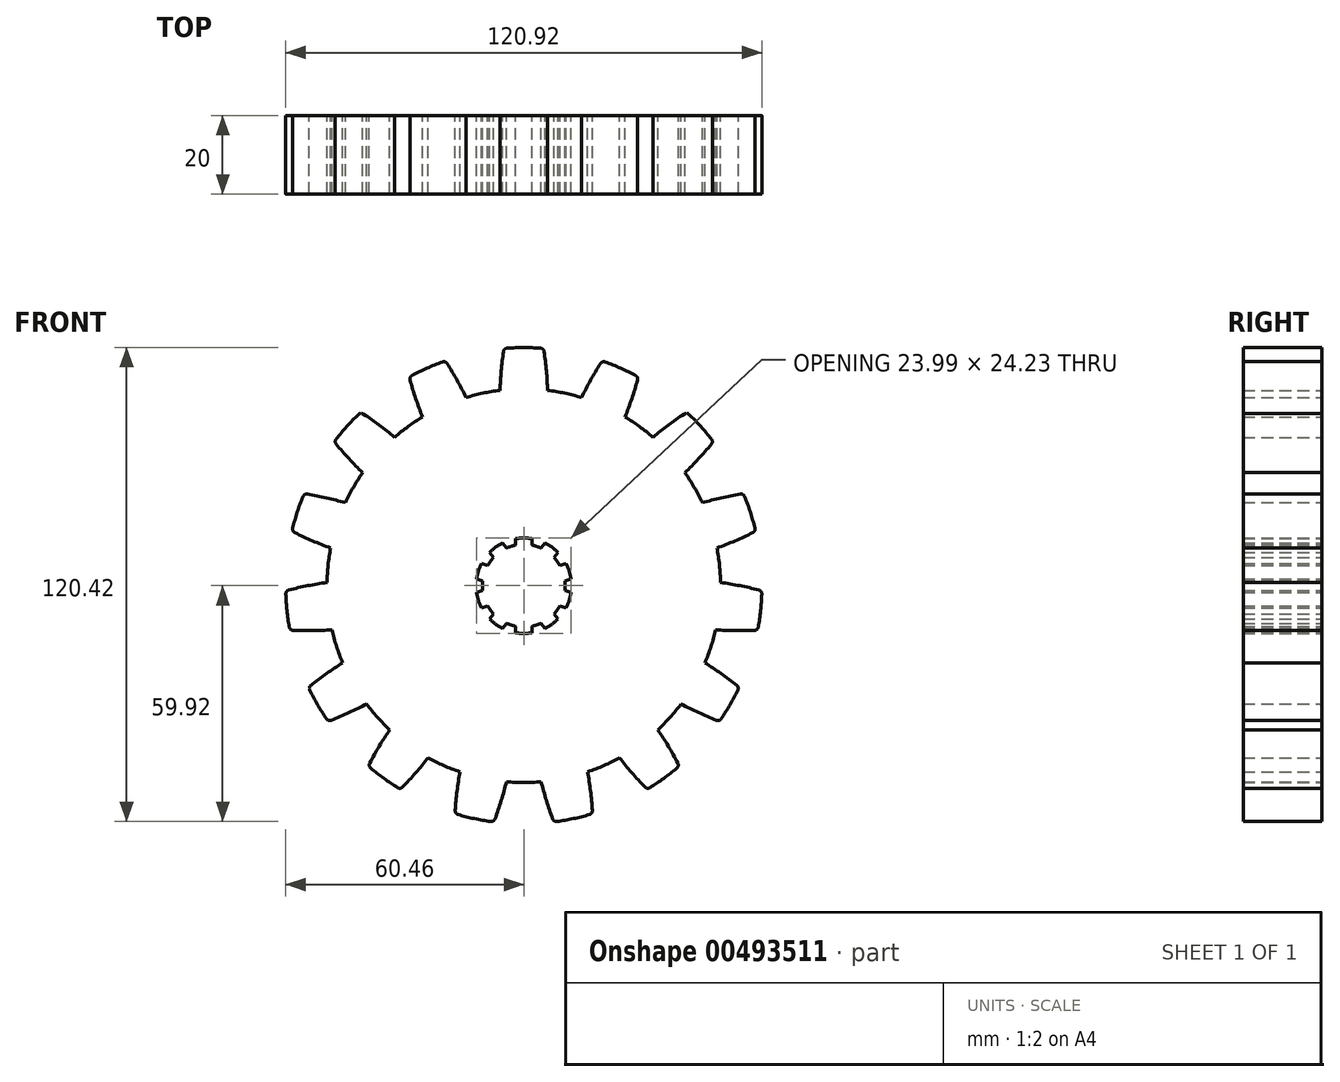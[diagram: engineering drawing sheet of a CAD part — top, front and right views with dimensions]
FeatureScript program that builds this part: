
annotation { "Feature Type Name" : "Feature", "Feature Type Description" : "" }
export const myFeature = defineFeature(function(context is Context, id is Id, definition is map)
    precondition{}
    {
        {
            var Q0;
            Q0=qCreatedBy(makeId("Front.planeOp"),FACE);
            var sketch = newSketch(context, id + "F0", { "sketchPlane" : qUnion([Q0])});
            skCircle(sketch, "E0", {"center": v(0, 0) * mm, "radius": 50 * mm});
            skCircle(sketch, "E1", {"center": v(0, 0) * mm, "radius": 10.5 * mm});
            skArc(sketch, "E2", {"start": v(2.05, 11.95) * mm, "mid": v(0, 12.12) * mm, "end": v(-2.05, 11.95) * mm});
            skLineSegment(sketch, "E3", {"start": v(-2.05, 11.95) * mm, "end": v(-2.05, 10.3) * mm});
            skLineSegment(sketch, "E4", {"start": v(2.05, 10.3) * mm, "end": v(2.05, 11.95) * mm});
            skArc(sketch, "E5", {"start": v(5.04, 60.29) * mm, "mid": v(0, 60.5) * mm, "end": v(-5.04, 60.29) * mm});
            skLineSegment(sketch, "E6", {"start": v(0, 50) * mm, "end": v(0, 46.5) * mm, "construction": true});
            skLineSegment(sketch, "E7", {"start": v(0, 46.5) * mm, "end": v(83.9, 46.5) * mm, "construction": true});
            skArc(sketch, "E8", {"start": v(-5.04, 60.29) * mm, "mid": v(-5.7, 54.98) * mm, "end": v(-6.05, 49.63) * mm});
            skArc(sketch, "E9.MirrorCS", {"start": v(5.04, 60.29) * mm, "mid": v(5.7, 54.98) * mm, "end": v(6.05, 49.63) * mm});
            skLineSegment(sketch, "E10.1.0", {"start": v(-4.4, 9.54) * mm, "end": v(-5.36, 10.87) * mm});
            skLineSegment(sketch, "E10.1.1", {"start": v(-8.68, 8.46) * mm, "end": v(-7.71, 7.13) * mm});
            skArc(sketch, "E10.1.2", {"start": v(-5.36, 10.87) * mm, "mid": v(-7.12, 9.8) * mm, "end": v(-8.68, 8.46) * mm});
            skLineSegment(sketch, "E10.2.0", {"start": v(-9.16, 5.13) * mm, "end": v(-10.73, 5.64) * mm});
            skLineSegment(sketch, "E10.2.1", {"start": v(-12, 1.74) * mm, "end": v(-10.43, 1.23) * mm});
            skArc(sketch, "E10.2.2", {"start": v(-10.73, 5.64) * mm, "mid": v(-11.52, 3.74) * mm, "end": v(-12, 1.74) * mm});
            skLineSegment(sketch, "E10.3.0", {"start": v(-10.43, -1.23) * mm, "end": v(-12, -1.74) * mm});
            skLineSegment(sketch, "E10.3.1", {"start": v(-10.73, -5.64) * mm, "end": v(-9.16, -5.13) * mm});
            skArc(sketch, "E10.3.2", {"start": v(-12, -1.74) * mm, "mid": v(-11.52, -3.74) * mm, "end": v(-10.73, -5.64) * mm});
            skLineSegment(sketch, "E10.4.0", {"start": v(-7.71, -7.13) * mm, "end": v(-8.68, -8.46) * mm});
            skLineSegment(sketch, "E10.4.1", {"start": v(-5.36, -10.87) * mm, "end": v(-4.4, -9.54) * mm});
            skArc(sketch, "E10.4.2", {"start": v(-8.68, -8.46) * mm, "mid": v(-7.12, -9.8) * mm, "end": v(-5.36, -10.87) * mm});
            skLineSegment(sketch, "E10.5.0", {"start": v(-2.05, -10.3) * mm, "end": v(-2.05, -11.95) * mm});
            skLineSegment(sketch, "E10.5.1", {"start": v(2.05, -11.95) * mm, "end": v(2.05, -10.3) * mm});
            skArc(sketch, "E10.5.2", {"start": v(-2.05, -11.95) * mm, "mid": v(0, -12.12) * mm, "end": v(2.05, -11.95) * mm});
            skLineSegment(sketch, "E10.6.0", {"start": v(4.4, -9.54) * mm, "end": v(5.36, -10.87) * mm});
            skLineSegment(sketch, "E10.6.1", {"start": v(8.68, -8.46) * mm, "end": v(7.71, -7.13) * mm});
            skArc(sketch, "E10.6.2", {"start": v(5.36, -10.87) * mm, "mid": v(7.12, -9.8) * mm, "end": v(8.68, -8.46) * mm});
            skLineSegment(sketch, "E10.7.0", {"start": v(9.16, -5.13) * mm, "end": v(10.73, -5.64) * mm});
            skLineSegment(sketch, "E10.7.1", {"start": v(12, -1.74) * mm, "end": v(10.43, -1.23) * mm});
            skArc(sketch, "E10.7.2", {"start": v(10.73, -5.64) * mm, "mid": v(11.52, -3.74) * mm, "end": v(12, -1.74) * mm});
            skLineSegment(sketch, "E10.8.0", {"start": v(10.43, 1.23) * mm, "end": v(12, 1.74) * mm});
            skLineSegment(sketch, "E10.8.1", {"start": v(10.73, 5.64) * mm, "end": v(9.16, 5.13) * mm});
            skArc(sketch, "E10.8.2", {"start": v(12, 1.74) * mm, "mid": v(11.52, 3.74) * mm, "end": v(10.73, 5.64) * mm});
            skLineSegment(sketch, "E10.9.0", {"start": v(7.71, 7.13) * mm, "end": v(8.68, 8.46) * mm});
            skLineSegment(sketch, "E10.9.1", {"start": v(5.36, 10.87) * mm, "end": v(4.4, 9.54) * mm});
            skArc(sketch, "E10.9.2", {"start": v(8.68, 8.46) * mm, "mid": v(7.12, 9.8) * mm, "end": v(5.36, 10.87) * mm});
            skSolve(sketch);
        }
        {
            var Q0;
            Q0=makeQuery(id+"F0.imprint","IMPRINT",FACE,{"disambiguationData":[TD([[makeQuery(id+"F0.imprint","IMPRINT",EDGE,{"derivedFrom":sQuery(id+"F0.wireOp",EDGE,"E5")}),1.0]])]});
            extrude(context, id + "F1", {"entities" : qUnion([Q0]), "depth" : 20 * mm});
        }
        {
            var Q0;
            Q0=makeQuery(id+"F0.imprint","IMPRINT",FACE,{"disambiguationData":[TD([[makeQuery(id+"F0.imprint","IMPRINT",EDGE,{"derivedFrom":sQuery(id+"F0.wireOp",EDGE,"E2")}),-1.0]])]});
            extrude(context, id + "F2", {"entities" : qUnion([Q0]), "depth" : 20 * mm});
        }
        {
            var Q0;
            Q0=makeQuery(id+"F1.opExtrude","SWEPT_EDGE",EDGE,{"disambiguationData":[OSD([sQuery(id+"F0.wireOp",EDGE,"E5"),sQuery(id+"F0.wireOp",EDGE,"E8")])]});
            var Q1;
            Q1=makeQuery(id+"F1.opExtrude","SWEPT_EDGE",EDGE,{"disambiguationData":[OSD([sQuery(id+"F0.wireOp",EDGE,"E5"),sQuery(id+"F0.wireOp",EDGE,"E9.MirrorCS")])]});
            fillet(context, id + "F3", {"entities" : qUnion([Q0, Q1]), "radius" : 1 * mm, "tangentPropagation" : true, "allowEdgeOverflow" : false});
        }
        {
            var Q0;
            Q0=makeQuery(id+"F1.opExtrude","SWEPT_BODY",BODY,{"disambiguationData":[OSD([sQuery(id+"F0.wireOp",EDGE,"E0"),sQuery(id+"F0.wireOp",EDGE,"E5"),sQuery(id+"F0.wireOp",EDGE,"E8"),sQuery(id+"F0.wireOp",EDGE,"E9.MirrorCS")])]});
            var Q1;
            Q1=sQuery(id+"F0.wireOp",EDGE,"E0");
            circularPattern(context, id + "F4", {"operationType" : NewBodyOperationType.ADD, "entities" : qUnion([Q0]), "axis" : qUnion([Q1]), "angle" : 360 * degree, "instanceCount" : 15, "equalSpace" : true});
        }
    });
